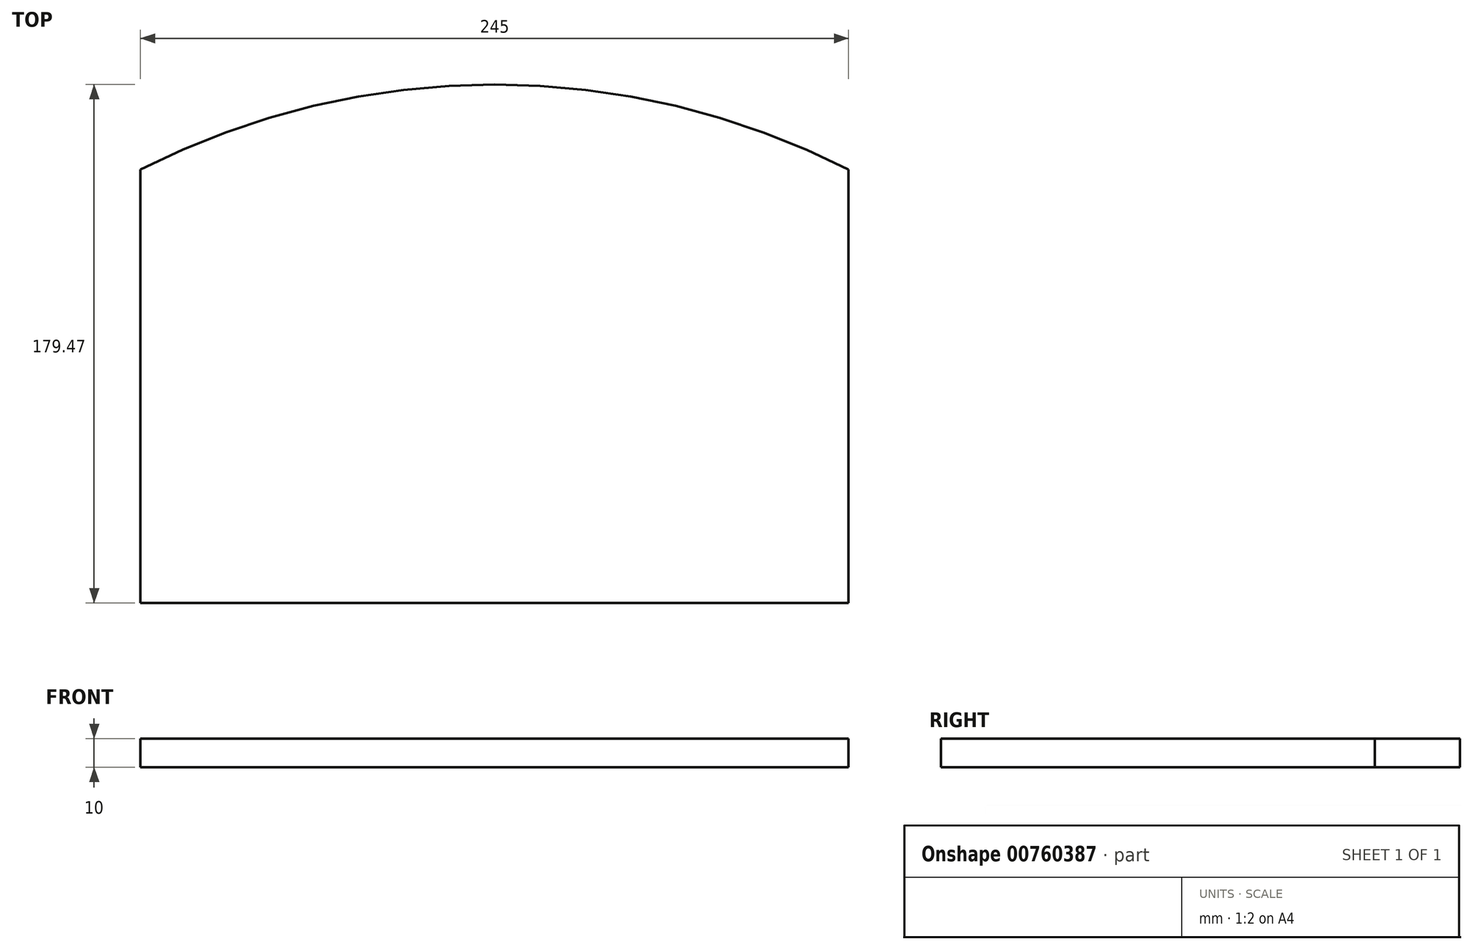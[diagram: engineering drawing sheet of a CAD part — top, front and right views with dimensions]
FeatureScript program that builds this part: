
annotation { "Feature Type Name" : "Feature", "Feature Type Description" : "" }
export const myFeature = defineFeature(function(context is Context, id is Id, definition is map)
    precondition{}
    {
        {
            var Q0;
            Q0=qCreatedBy(makeId("Top.planeOp"),FACE);
            var sketch = newSketch(context, id + "F0", { "sketchPlane" : qUnion([Q0])});
            skPoint(sketch, "E0", {"position": v(151.1, 154.93) * mm});
            skPoint(sketch, "E1", {"position": v(140, 77.47) * mm});
            skPoint(sketch, "E2", {"position": v(146.5, 0) * mm});
            skPoint(sketch, "E3", {"position": v(0, 210) * mm});
            skPoint(sketch, "E4", {"position": v(72.86, 179.48) * mm});
            skPoint(sketch, "E5", {"position": v(-38.35, 186.04) * mm});
            skPoint(sketch, "E6", {"position": v(-24.12, 200) * mm});
            skPoint(sketch, "E7", {"position": v(-154.5, 163.42) * mm});
            skLineSegment(sketch, "E8", {"start": v(0, 210) * mm, "end": v(0, -300) * mm, "construction": true});
            skPoint(sketch, "E9.MirrorP", {"position": v(-72.86, 179.48) * mm});
            skPoint(sketch, "E10.MirrorP", {"position": v(-151.1, 154.93) * mm});
            skPoint(sketch, "E11.MirrorP", {"position": v(-140, 77.47) * mm});
            skPoint(sketch, "E12.MirrorP", {"position": v(-146.5, 0) * mm});
            skPoint(sketch, "E13", {"position": v(0, 0) * mm});
            skPoint(sketch, "E14.MirrorP", {"position": v(154.5, 163.42) * mm});
            skPoint(sketch, "E15.MirrorP", {"position": v(38.35, 186.04) * mm});
            skPoint(sketch, "E16.MirrorP", {"position": v(24.12, 200) * mm});
            skPoint(sketch, "E17", {"position": v(-111.22, 185.44) * mm});
            skPoint(sketch, "E18.MirrorP", {"position": v(111.21, 185.44) * mm});
            skLineSegment(sketch, "E19", {"start": v(-146.5, 0) * mm, "end": v(146.5, 0) * mm});
            skPoint(sketch, "E20", {"position": v(0, 193.84) * mm});
            skPoint(sketch, "E21", {"position": v(-120.16, 190.34) * mm});
            skPoint(sketch, "E22", {"position": v(-131.3, 192.59) * mm});
            skPoint(sketch, "E23", {"position": v(-143.04, 189.12) * mm});
            skPoint(sketch, "E24", {"position": v(-150.16, 182.65) * mm});
            skPoint(sketch, "E25", {"position": v(-153.61, 176.08) * mm});
            skPoint(sketch, "E26", {"position": v(-154.92, 169.2) * mm});
            skPoint(sketch, "E27.MirrorP", {"position": v(120.16, 190.34) * mm});
            skPoint(sketch, "E28.MirrorP", {"position": v(131.3, 192.59) * mm});
            skPoint(sketch, "E29.MirrorP", {"position": v(143.04, 189.12) * mm});
            skPoint(sketch, "E30.MirrorP", {"position": v(150.16, 182.65) * mm});
            skPoint(sketch, "E31.MirrorP", {"position": v(153.61, 176.08) * mm});
            skPoint(sketch, "E32.MirrorP", {"position": v(154.92, 169.2) * mm});
            skFitSpline(sketch, "E33", {"points": [v(-146.5, 0) * mm, v(-140, 77.47) * mm, v(-151.1, 154.93) * mm, v(-154.5, 163.42) * mm, v(-154.92, 169.2) * mm, v(-153.61, 176.08) * mm, v(-150.16, 182.65) * mm, v(-143.04, 189.12) * mm, v(-131.3, 192.59) * mm, v(-120.16, 190.34) * mm, v(-111.22, 185.44) * mm, v(-72.87, 179.48) * mm, v(-38.35, 186.04) * mm, v(-24.12, 200) * mm, v(0, 210) * mm, v(24.12, 200) * mm, v(38.35, 186.04) * mm, v(72.86, 179.48) * mm, v(111.21, 185.44) * mm, v(120.16, 190.34) * mm, v(131.3, 192.59) * mm, v(143.04, 189.12) * mm, v(150.16, 182.65) * mm, v(153.61, 176.08) * mm, v(154.92, 169.2) * mm, v(154.5, 163.42) * mm, v(151.1, 154.93) * mm, v(140, 77.47) * mm, v(146.5, 0) * mm], "startDerivative": vector(163.85, 1049.48) * mm, "endDerivative": vector(163.85, -1049.48) * mm});
            skLineSegment(sketch, "E34.bottom", {"start": v(-107.5, 0) * mm, "end": v(107.5, 0) * mm});
            skSolve(sketch);
        }
        {
            var Q0;
            Q0=qCreatedBy(makeId("Top.planeOp"),FACE);
            cPlane(context, id + "F1", {"entities" : qUnion([Q0]), "cplaneType" : CPlaneType.OFFSET, "offset" : 100 * mm, "width" : 150 * mm, "height" : 150 * mm});
        }
        {
            var Q0;
            Q0=qCreatedBy(id+"F1.planeOp",FACE);
            var sketch = newSketch(context, id + "F2", { "sketchPlane" : qUnion([Q0])});
            skPoint(sketch, "E35.0", {"position": v(-146.5, 0) * mm});
            skPoint(sketch, "E36", {"position": v(-150, 128) * mm});
            skPoint(sketch, "E37", {"position": v(-15, 206) * mm});
            skPoint(sketch, "E38", {"position": v(-83.69, 183.02) * mm});
            skPoint(sketch, "E39", {"position": v(-57.22, 198) * mm});
            skPoint(sketch, "E40.16.internal.orphan", {"position": v(-102.04, 172) * mm});
            skPoint(sketch, "E40.2.internal.orphan", {"position": v(-150, 60) * mm});
            skLineSegment(sketch, "E41", {"start": v(-146.5, 0) * mm, "end": v(146.5, 0) * mm});
            skLineSegment(sketch, "E42", {"start": v(0, 0) * mm, "end": v(0, 210) * mm, "construction": true});
            skPoint(sketch, "E42.endSnap0", {"position": v(0, 0) * mm});
            skLineSegment(sketch, "E43", {"start": v(214.08, 0) * mm, "end": v(-299.05, 0) * mm, "construction": true});
            skPoint(sketch, "E44.10.internal.orphan", {"position": v(-151, 176) * mm});
            skPoint(sketch, "E44.11.internal.orphan", {"position": v(-138, 182) * mm});
            skPoint(sketch, "E44.12.internal.orphan", {"position": v(-116, 173) * mm});
            skPoint(sketch, "E44.15.internal.orphan", {"position": v(-67.88, 193.66) * mm});
            skPoint(sketch, "E44.17.internal.orphan", {"position": v(-46.27, 200) * mm});
            skPoint(sketch, "E44.18.internal.orphan", {"position": v(-38.42, 198) * mm});
            skPoint(sketch, "E44.19.internal.orphan", {"position": v(-34.04, 196) * mm});
            skPoint(sketch, "E44.2.internal.orphan", {"position": v(-145, 100) * mm});
            skPoint(sketch, "E44.20.internal.orphan", {"position": v(-29, 195) * mm});
            skPoint(sketch, "E44.21.internal.orphan", {"position": v(-25, 198) * mm});
            skPoint(sketch, "E44.3.internal.orphan", {"position": v(-150, 121) * mm});
            skPoint(sketch, "E44.5.internal.orphan", {"position": v(-149, 133) * mm});
            skPoint(sketch, "E44.6.internal.orphan", {"position": v(-147.5, 139) * mm});
            skPoint(sketch, "E44.7.internal.orphan", {"position": v(-149, 145) * mm});
            skPoint(sketch, "E44.8.internal.orphan", {"position": v(-153, 151) * mm});
            skPoint(sketch, "E44.9.internal.orphan", {"position": v(-157, 163) * mm});
            skPoint(sketch, "E45.MirrorP", {"position": v(15, 206) * mm});
            skPoint(sketch, "E46.MirrorP", {"position": v(29, 195) * mm});
            skPoint(sketch, "E47.MirrorP", {"position": v(102.04, 172) * mm});
            skPoint(sketch, "E48.MirrorP", {"position": v(83.69, 183.02) * mm});
            skPoint(sketch, "E49.MirrorP", {"position": v(46.27, 200) * mm});
            skPoint(sketch, "E50.MirrorP", {"position": v(25, 198) * mm});
            skPoint(sketch, "E51.MirrorP", {"position": v(149, 133) * mm});
            skPoint(sketch, "E52.MirrorP", {"position": v(151, 176) * mm});
            skPoint(sketch, "E53.MirrorP", {"position": v(149, 145) * mm});
            skPoint(sketch, "E54.MirrorP", {"position": v(150, 60) * mm});
            skPoint(sketch, "E55.MirrorP", {"position": v(150, 128) * mm});
            skPoint(sketch, "E56.MirrorP", {"position": v(145, 100) * mm});
            skPoint(sketch, "E57.MirrorP", {"position": v(38.42, 198) * mm});
            skPoint(sketch, "E58.MirrorP", {"position": v(67.88, 193.66) * mm});
            skPoint(sketch, "E59.MirrorP", {"position": v(153, 151) * mm});
            skPoint(sketch, "E60.MirrorP", {"position": v(150, 121) * mm});
            skPoint(sketch, "E61.MirrorP", {"position": v(57.22, 198) * mm});
            skPoint(sketch, "E62.MirrorP", {"position": v(116, 173) * mm});
            skPoint(sketch, "E63.MirrorP", {"position": v(138, 182) * mm});
            skPoint(sketch, "E64.MirrorP", {"position": v(147.5, 139) * mm});
            skPoint(sketch, "E65.MirrorP", {"position": v(157, 163) * mm});
            skPoint(sketch, "E66.MirrorP", {"position": v(34.04, 196) * mm});
            skPoint(sketch, "E67", {"position": v(-123.4, 176.5) * mm});
            skPoint(sketch, "E68", {"position": v(-128, 180) * mm});
            skPoint(sketch, "E69.MirrorP", {"position": v(123.4, 176.5) * mm});
            skPoint(sketch, "E70.MirrorP", {"position": v(128, 180) * mm});
            skFitSpline(sketch, "E71", {"points": [v(-146.5, 0) * mm, v(-150, 60) * mm, v(-145, 100) * mm, v(-150, 121) * mm, v(-150, 128) * mm, v(-149, 133) * mm, v(-147.5, 139) * mm, v(-149, 145) * mm, v(-153, 151) * mm, v(-157, 163) * mm, v(-151, 176) * mm, v(-138, 182) * mm, v(-128, 180) * mm, v(-123.4, 176.5) * mm, v(-116, 173) * mm, v(-102.04, 172) * mm, v(-83.69, 183.02) * mm, v(-67.88, 193.66) * mm, v(-57.22, 198) * mm, v(-46.27, 200) * mm, v(-38.42, 198) * mm, v(-34.04, 196) * mm, v(-29, 195) * mm, v(-25, 198) * mm, v(-15, 206) * mm, v(0, 210) * mm, v(15, 206) * mm, v(25, 198) * mm, v(29, 195) * mm, v(34.04, 196) * mm, v(38.42, 198) * mm, v(46.27, 200) * mm, v(57.22, 198) * mm, v(67.88, 193.66) * mm, v(83.69, 183.02) * mm, v(102.04, 172) * mm, v(116, 173) * mm, v(123.4, 176.5) * mm, v(128, 180) * mm, v(138, 182) * mm, v(151, 176) * mm, v(157, 163) * mm, v(153, 151) * mm, v(149, 145) * mm, v(147.5, 139) * mm, v(149, 133) * mm, v(150, 128) * mm, v(150, 121) * mm, v(145, 100) * mm, v(150, 60) * mm, v(146.5, 0) * mm], "startDerivative": vector(-209.03, 1625.36) * mm, "endDerivative": vector(-209.03, -1625.36) * mm});
            skEllipse(sketch, "E72", {"center": v(0, 190) * mm, "majorRadius": 5 * mm, "minorRadius": 3.75 * mm, "majorAxis": v(1, 0)});
            skLineSegment(sketch, "E73", {"start": v(122.5, 0) * mm, "end": v(122.5, 150) * mm});
            skLineSegment(sketch, "E74", {"start": v(122.5, 150) * mm, "end": v(-122.5, 150) * mm});
            skLineSegment(sketch, "E75", {"start": v(-122.5, 150) * mm, "end": v(-122.5, 0) * mm});
            skLineSegment(sketch, "E76", {"start": v(-122.5, 0) * mm, "end": v(122.5, 0) * mm});
            skCircle(sketch, "E77", {"center": v(0, -89.9) * mm, "radius": 269.36 * mm});
            skPoint(sketch, "E77.third.point", {"position": v(0, -359.25) * mm});
            skSolve(sketch);
        }
        {
            var Q0;
            Q0=makeQuery(id+"F2.imprint","IMPRINT",FACE,{"disambiguationData":[TD([[makeQuery(id+"F2.imprint","IMPRINT",EDGE,{"derivedFrom":sQuery(id+"F2.wireOp",EDGE,"E73")}),1.0]])]});
            var Q1;
            {var subQ0=sQuery(id+"F2.wireOp",EDGE,"E74");Q1=makeQuery(id+"F2.imprint","IMPRINT",FACE,{"disambiguationData":[TD([[makeQuery(id+"F2.imprint","IMPRINT",EDGE,{"derivedFrom":subQ0}),-1.0]])]});}
            extrude(context, id + "F3", {"entities" : qUnion([Q0, Q1]), "depth" : 10 * mm, "offsetDistance" : 25 * mm});
        }
    });
